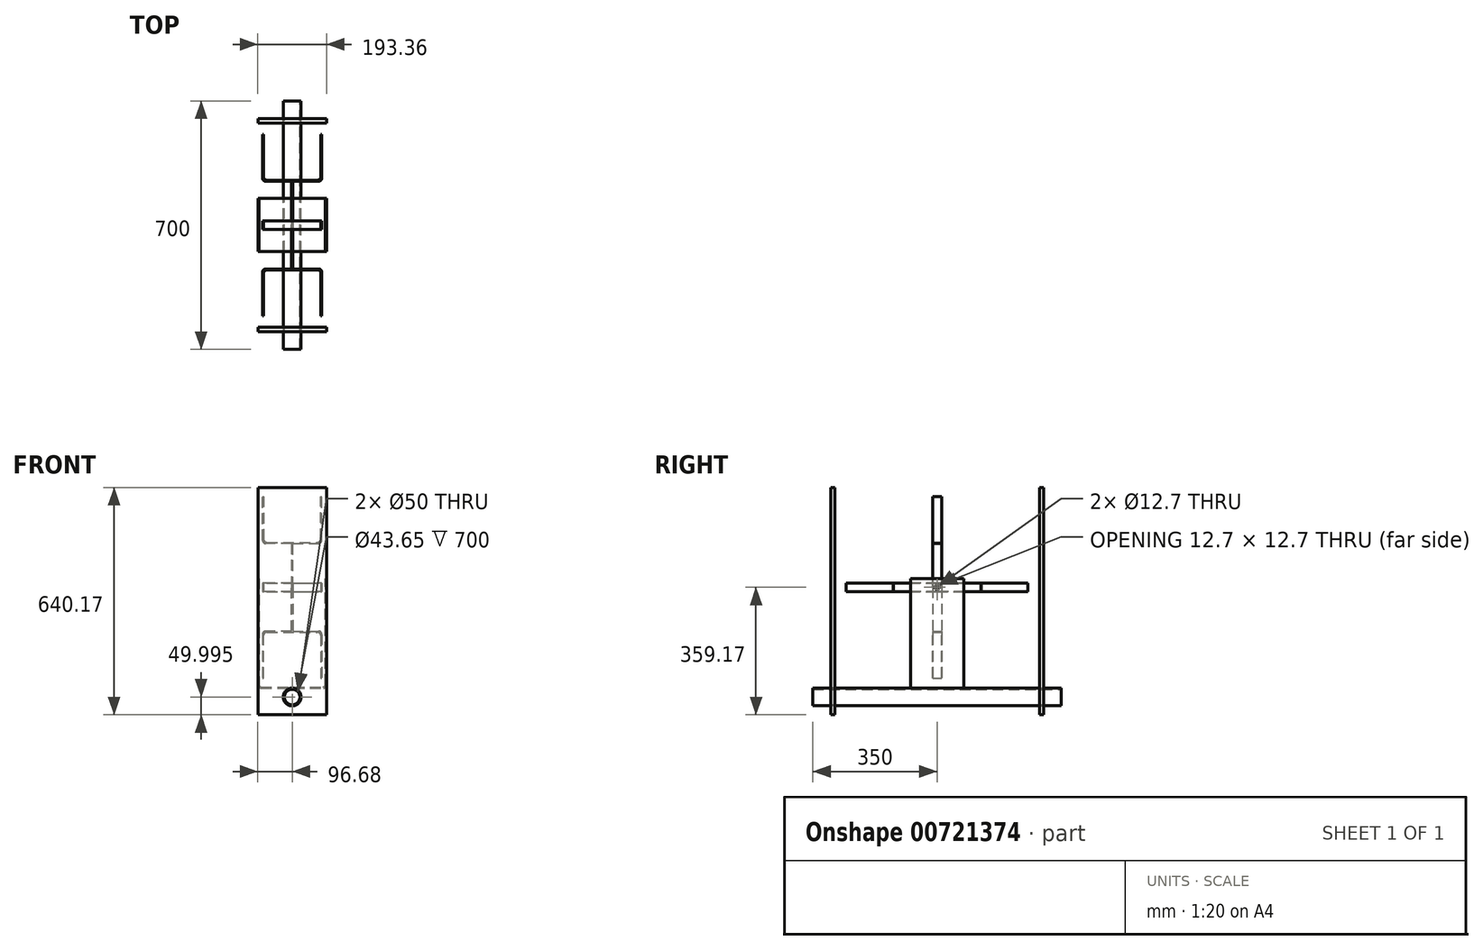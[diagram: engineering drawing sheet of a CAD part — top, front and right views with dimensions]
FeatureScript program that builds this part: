
annotation { "Feature Type Name" : "Feature", "Feature Type Description" : "" }
export const myFeature = defineFeature(function(context is Context, id is Id, definition is map)
    precondition{}
    {
        {
            var Q0;
            Q0=qCreatedBy(makeId("Right.planeOp"),FACE);
            var sketch = newSketch(context, id + "F0", { "sketchPlane" : qUnion([Q0])});
            skLineSegment(sketch, "E0", {"start": v(-75, 0) * mm, "end": v(75, 0) * mm});
            skLineSegment(sketch, "E1", {"start": v(75, 0) * mm, "end": v(75, -3.18) * mm});
            skLineSegment(sketch, "E2", {"start": v(75, -3.17) * mm, "end": v(-75, -3.17) * mm});
            skLineSegment(sketch, "E3", {"start": v(-75, -3.18) * mm, "end": v(-75, 0) * mm});
            skSolve(sketch);
        }
        {
            var Q0;
            Q0=qCreatedBy(makeId("Front.planeOp"),FACE);
            var sketch = newSketch(context, id + "F1", { "sketchPlane" : qUnion([Q0])});
            skLineSegment(sketch, "E4", {"start": v(-93.5, 306) * mm, "end": v(-93.5, 6) * mm});
            skLineSegment(sketch, "E5", {"start": v(-87.5, 0) * mm, "end": v(87.5, 0) * mm});
            skLineSegment(sketch, "E6", {"start": v(93.5, 6) * mm, "end": v(93.5, 306) * mm});
            skPoint(sketch, "E7.visualSharp", {"position": v(-93.5, 0) * mm});
            skArc(sketch, "E7.filletArc", {"start": v(-93.5, 6) * mm, "mid": v(-91.74, 1.76) * mm, "end": v(-87.5, 0) * mm});
            skPoint(sketch, "E8.visualSharp", {"position": v(93.5, 0) * mm});
            skArc(sketch, "E8.filletArc", {"start": v(87.5, 0) * mm, "mid": v(91.74, 1.76) * mm, "end": v(93.5, 6) * mm});
            skSolve(sketch);
        }
        {
            var Q0;
            Q0 = qSketchRegion(id + "F0", true);
            var Q1;
            Q1 = qConstructionFilter(qBodyType(qCreatedBy(id + "F1" ,EDGE), BodyType.WIRE), ConstructionObject.NO);
            sweep(context, id + "F2", {"profiles" : qUnion([Q0]), "path" : qUnion([Q1])});
        }
        {
            var Q0;
            Q0=makeQuery(id+"F2.opSweep","SWEPT_FACE",FACE,{"disambiguationData":[OSD([sQuery(id+"F0.wireOp",EDGE,"E2"),sQuery(id+"F1.wireOp",EDGE,"E6")])]});
            var sketch = newSketch(context, id + "F3", { "sketchPlane" : qUnion([Q0])});
            skCircle(sketch, "E9", {"center": v(0, 281) * mm, "radius": 6.35 * mm});
            skSolve(sketch);
        }
        {
            var Q0;
            Q0 = qSketchRegion(id + "F3", true);
            extrude(context, id + "F4", {"entities" : qUnion([Q0]), "operationType" : NewBodyOperationType.REMOVE, "endBound" : BoundingType.THROUGH_ALL, "oppositeDirection" : true, "depth" : 25 * mm, "offsetDistance" : 25 * mm});
        }
        {
            var Q0;
            Q0=qCreatedBy(makeId("Front.planeOp"),FACE);
            var sketch = newSketch(context, id + "F5", { "sketchPlane" : qUnion([Q0])});
            skLineSegment(sketch, "E10", {"start": v(0, 281) * mm, "end": v(-93.5, 281) * mm, "construction": true});
            skLineSegment(sketch, "E11.0", {"start": v(-93.5, 287.35) * mm, "end": v(-93.5, 274.65) * mm, "construction": true});
            skLineSegment(sketch, "E12", {"start": v(0, 281) * mm, "end": v(0, 157.5) * mm, "construction": true});
            skLineSegment(sketch, "E13", {"start": v(0, 157.5) * mm, "end": v(-74.5, 157.5) * mm});
            skLineSegment(sketch, "E14", {"start": v(-83.5, 148.5) * mm, "end": v(-83.5, 25) * mm});
            skLineSegment(sketch, "E15.MirrorCS", {"start": v(0, 157.5) * mm, "end": v(74.5, 157.5) * mm});
            skLineSegment(sketch, "E16.MirrorCS", {"start": v(83.5, 148.5) * mm, "end": v(83.5, 25) * mm});
            skLineSegment(sketch, "E17", {"start": v(-83.5, 25) * mm, "end": v(-80.33, 25) * mm});
            skLineSegment(sketch, "E18", {"start": v(-80.33, 25) * mm, "end": v(-80.33, 145.32) * mm});
            skLineSegment(sketch, "E19", {"start": v(-71.33, 154.32) * mm, "end": v(71.33, 154.32) * mm});
            skLineSegment(sketch, "E20", {"start": v(80.33, 145.32) * mm, "end": v(80.33, 25) * mm});
            skLineSegment(sketch, "E21", {"start": v(80.33, 25) * mm, "end": v(83.5, 25) * mm});
            skLineSegment(sketch, "E22", {"start": v(-1.59, 157.5) * mm, "end": v(-1.59, 281) * mm});
            skLineSegment(sketch, "E23", {"start": v(-1.59, 281) * mm, "end": v(1.59, 281) * mm});
            skLineSegment(sketch, "E24", {"start": v(1.59, 281) * mm, "end": v(1.59, 157.5) * mm});
            skPoint(sketch, "E25.visualSharp", {"position": v(83.5, 157.5) * mm});
            skArc(sketch, "E25.filletArc", {"start": v(83.5, 148.5) * mm, "mid": v(80.86, 154.86) * mm, "end": v(74.5, 157.5) * mm});
            skPoint(sketch, "E26.visualSharp", {"position": v(-80.33, 154.32) * mm});
            skArc(sketch, "E26.filletArc", {"start": v(-71.33, 154.32) * mm, "mid": v(-77.69, 151.69) * mm, "end": v(-80.33, 145.32) * mm});
            skPoint(sketch, "E27.visualSharp", {"position": v(-83.5, 157.5) * mm});
            skArc(sketch, "E27.filletArc", {"start": v(-74.5, 157.5) * mm, "mid": v(-80.86, 154.86) * mm, "end": v(-83.5, 148.5) * mm});
            skPoint(sketch, "E28.visualSharp", {"position": v(80.33, 154.32) * mm});
            skArc(sketch, "E28.filletArc", {"start": v(80.33, 145.32) * mm, "mid": v(77.69, 151.69) * mm, "end": v(71.33, 154.32) * mm});
            skSolve(sketch);
        }
        {
            var Q0;
            Q0 = qSketchRegion(id + "F5", true);
            extrude(context, id + "F6", {"entities" : qUnion([Q0]), "depth" : 25 * mm, "offsetDistance" : 25 * mm, "symmetric" : true});
        }
        {
            var Q0;
            Q0=makeQuery(id+"F6.opExtrude","SWEPT_BODY",BODY,{"disambiguationData":[OSD([sQuery(id+"F5.wireOp",EDGE,"E13"),sQuery(id+"F5.wireOp",EDGE,"E14"),sQuery(id+"F5.wireOp",EDGE,"E15.MirrorCS"),sQuery(id+"F5.wireOp",EDGE,"E16.MirrorCS"),sQuery(id+"F5.wireOp",EDGE,"E17"),sQuery(id+"F5.wireOp",EDGE,"E18"),sQuery(id+"F5.wireOp",EDGE,"E19"),sQuery(id+"F5.wireOp",EDGE,"E20"),sQuery(id+"F5.wireOp",EDGE,"E21"),sQuery(id+"F5.wireOp",EDGE,"E22"),sQuery(id+"F5.wireOp",EDGE,"E23"),sQuery(id+"F5.wireOp",EDGE,"E24")])]});
            var Q1;
            Q1=makeQuery(id+"F4.boolean.opBoolean","INTERSECT",EDGE,{"derivedFrom":[makeQuery(id+"F2.opSweep","SWEPT_FACE",FACE,{"disambiguationData":[OSD([sQuery(id+"F0.wireOp",EDGE,"E0"),sQuery(id+"F1.wireOp",EDGE,"E4")])]}),makeQuery(id+"F4.opExtrude","SWEPT_FACE",FACE,{"disambiguationData":[OSD([sQuery(id+"F3.wireOp",EDGE,"E9")])]})]});
            circularPattern(context, id + "F7", {"entities" : qUnion([Q0]), "axis" : qUnion([Q1]), "angle" : 360 * degree, "instanceCount" : 4, "equalSpace" : true});
        }
        {
            var Q0;
            Q0=qCreatedBy(makeId("Front.planeOp"),FACE);
            var sketch = newSketch(context, id + "F8", { "sketchPlane" : qUnion([Q0])});
            skCircle(sketch, "E29", {"center": v(0, -28.17) * mm, "radius": 25 * mm});
            skCircle(sketch, "E30", {"center": v(0, -28.17) * mm, "radius": 21.82 * mm});
            skLineSegment(sketch, "E31.0.0", {"start": v(-87.5, -3.17) * mm, "end": v(87.5, -3.17) * mm});
            skLineSegment(sketch, "E31.0.2", {"start": v(87.5, -3.18) * mm, "end": v(-87.5, -3.18) * mm, "construction": true});
            skSolve(sketch);
        }
        {
            var Q0;
            Q0 = qSketchRegion(id + "F8", true);
            extrude(context, id + "F9", {"entities" : qUnion([Q0]), "depth" : 700 * mm, "offsetDistance" : 25 * mm, "symmetric" : true});
        }
        {
            var Q0;
            Q0=qCreatedBy(makeId("Front.planeOp"),FACE);
            cPlane(context, id + "F10", {"entities" : qUnion([Q0]), "cplaneType" : CPlaneType.OFFSET, "offset" : 300 * mm, "width" : 150 * mm, "height" : 150 * mm});
        }
        {
            var Q0;
            Q0=qCreatedBy(id+"F10.planeOp",FACE);
            var sketch = newSketch(context, id + "F11", { "sketchPlane" : qUnion([Q0])});
            skCircle(sketch, "E32.0", {"center": v(0, -28.17) * mm, "radius": 25 * mm});
            skLineSegment(sketch, "E33.bottom", {"start": v(-96.67, -78.17) * mm, "end": v(96.68, -78.17) * mm});
            skLineSegment(sketch, "E33.top", {"start": v(-96.68, 562) * mm, "end": v(96.67, 562) * mm});
            skLineSegment(sketch, "E33.left", {"start": v(-96.67, -78.17) * mm, "end": v(-96.68, 562) * mm});
            skLineSegment(sketch, "E33.right", {"start": v(96.68, -78.17) * mm, "end": v(96.67, 562) * mm});
            skSolve(sketch);
        }
        {
            var Q0;
            Q0 = qSketchRegion(id + "F11", true);
            extrude(context, id + "F12", {"entities" : qUnion([Q0]), "oppositeDirection" : true, "depth" : 12 * mm, "offsetDistance" : 25 * mm});
        }
        {
            var Q0;
            Q0=makeQuery(id+"F12.opExtrude","SWEPT_BODY",BODY,{"disambiguationData":[OSD([sQuery(id+"F11.wireOp",EDGE,"E32.0"),sQuery(id+"F11.wireOp",EDGE,"E33.bottom"),sQuery(id+"F11.wireOp",EDGE,"E33.top"),sQuery(id+"F11.wireOp",EDGE,"E33.left"),sQuery(id+"F11.wireOp",EDGE,"E33.right")])]});
            var Q1;
            Q1=qCreatedBy(makeId("Front.planeOp"),FACE);
            mirror(context, id + "F13", {"entities" : qUnion([Q0]), "mirrorPlane" : qUnion([Q1])});
        }
    });
